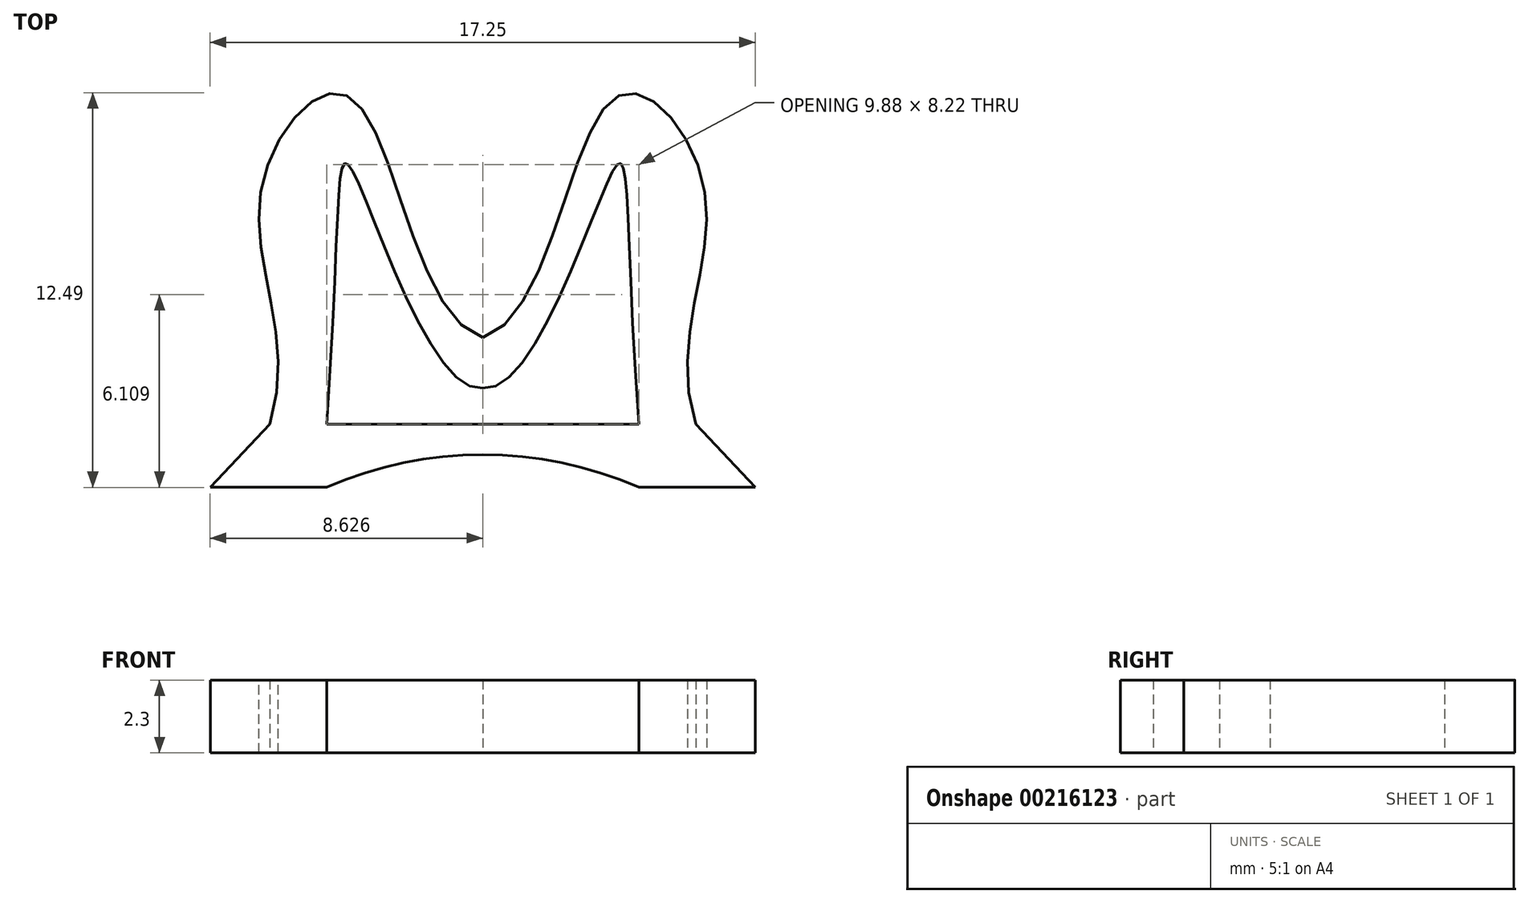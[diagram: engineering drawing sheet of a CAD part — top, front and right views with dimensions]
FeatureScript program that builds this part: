
annotation { "Feature Type Name" : "Feature", "Feature Type Description" : "" }
export const myFeature = defineFeature(function(context is Context, id is Id, definition is map)
    precondition{}
    {
        {
            var Q0;
            Q0=qCreatedBy(makeId("Top.planeOp"),FACE);
            var sketch = newSketch(context, id + "F0", { "sketchPlane" : qUnion([Q0])});
            skLineSegment(sketch, "E0", {"start": v(-5.54, -5.35) * mm, "end": v(-3.73, -5.35) * mm});
            skFitSpline(sketch, "E1.MirrorCS", {"points": [v(-5.54, -5.35) * mm, v(-5.8, 2.17) * mm, v(-3, 5) * mm, v(1.2, -2.6) * mm], "startDerivative": vector(7.4, 23.56) * mm, "endDerivative": vector(17.16, -4.9) * mm});
            skFitSpline(sketch, "E2", {"points": [v(-3.73, -5.35) * mm, v(-2.81, 2.47) * mm, v(1.2, -4.21) * mm], "startDerivative": vector(2.92, 41.73) * mm, "endDerivative": vector(9.45, 1.33) * mm});
            skLineSegment(sketch, "E3.MirrorCS", {"start": v(7.95, -5.35) * mm, "end": v(6.15, -5.35) * mm});
            skLineSegment(sketch, "E4", {"start": v(-5.42, -7.35) * mm, "end": v(-7.42, -7.35) * mm});
            skLineSegment(sketch, "E5", {"start": v(-7.42, -7.35) * mm, "end": v(-5.54, -5.35) * mm});
            skLineSegment(sketch, "E6", {"start": v(7.83, -7.35) * mm, "end": v(9.83, -7.35) * mm});
            skLineSegment(sketch, "E7", {"start": v(9.83, -7.35) * mm, "end": v(7.95, -5.35) * mm});
            skLineSegment(sketch, "E8", {"start": v(-3.73, -5.35) * mm, "end": v(6.15, -5.35) * mm});
            skArc(sketch, "E9", {"start": v(6.15, -7.35) * mm, "mid": v(1.2, -6.31) * mm, "end": v(-3.73, -7.35) * mm});
            skLineSegment(sketch, "E10", {"start": v(-5.42, -7.35) * mm, "end": v(-3.73, -7.35) * mm});
            skLineSegment(sketch, "E11", {"start": v(6.15, -7.35) * mm, "end": v(7.83, -7.35) * mm});
            skLineSegment(sketch, "E12", {"start": v(1.2, 6.93) * mm, "end": v(1.2, -11.27) * mm, "construction": true});
            skFitSpline(sketch, "E13.MirrorCS", {"points": [v(6.15, -5.35) * mm, v(5.23, 2.47) * mm, v(1.2, -4.21) * mm], "startDerivative": vector(-2.92, 41.73) * mm, "endDerivative": vector(-9.45, 1.33) * mm});
            skFitSpline(sketch, "E14.MirrorCS", {"points": [v(7.95, -5.35) * mm, v(8.2, 2.17) * mm, v(5.42, 5) * mm, v(1.2, -2.6) * mm], "startDerivative": vector(-7.4, 23.56) * mm, "endDerivative": vector(-17.16, -4.9) * mm});
            skFitSpline(sketch, "E15.MirrorCS", {"points": [v(6.15, -5.35) * mm, v(5.23, 2.47) * mm, v(1.2, -4.21) * mm], "startDerivative": vector(-2.92, 41.73) * mm, "endDerivative": vector(-9.45, 1.33) * mm});
            skFitSpline(sketch, "E16.MirrorCS", {"points": [v(-3.73, -5.35) * mm, v(-2.81, 2.47) * mm, v(1.2, -4.21) * mm], "startDerivative": vector(2.92, 41.73) * mm, "endDerivative": vector(9.45, 1.33) * mm});
            skLineSegment(sketch, "E17", {"start": v(-5.88, 1.28) * mm, "end": v(-5.8, -11.55) * mm, "construction": true});
            skLineSegment(sketch, "E18.MirrorCS", {"start": v(8.3, 1.28) * mm, "end": v(8.2, -11.55) * mm, "construction": true});
            skPoint(sketch, "E19", {"position": v(-4.8, 4.3) * mm});
            skPoint(sketch, "E20.MirrorP", {"position": v(7.2, 4.3) * mm});
            skSolve(sketch);
        }
        {
            var Q0;
            Q0 = qSketchRegion(id + "F0", true);
            extrude(context, id + "F1", {"entities" : qUnion([Q0]), "depth" : 2.3 * mm});
        }
    });
